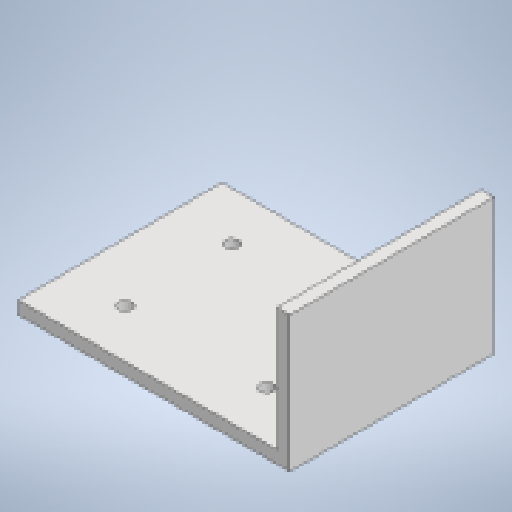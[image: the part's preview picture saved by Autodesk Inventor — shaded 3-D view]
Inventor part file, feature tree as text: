
AUTODESK INVENTOR PART (.ipt)
format: ipt  version: 2023 (Build 270158000, 158)  size: 141,312 bytes
history: native  units: in
note: dims shown in document units (in); Inventor stores cm internally (conversion verified against a paired STEP export)
features: extrude x2, sketch x2
ambient origin geometry x8: Origin, YZ Plane, XZ Plane, XY Plane, X Axis, Y Axis, Z Axis, Center Point
bodies: Solid1 (feature_tree)
feature tree (4):
  extrude  "Extrusion1"  Depth=2.0in
  extrude  "Extrusion2"  Depth=3.0in TaperAngle=0.0deg
  sketch  "Sketch1"  dims[d0=4.0in d1=2.0in]
  sketch  "Sketch2"  dims[d2=0.1875in d3=3.0in d4=0.0in d5=2.0866in d6=1.5748in d7=2.2126in d8=0.1969in d9=3.0in d10=0.0in]
